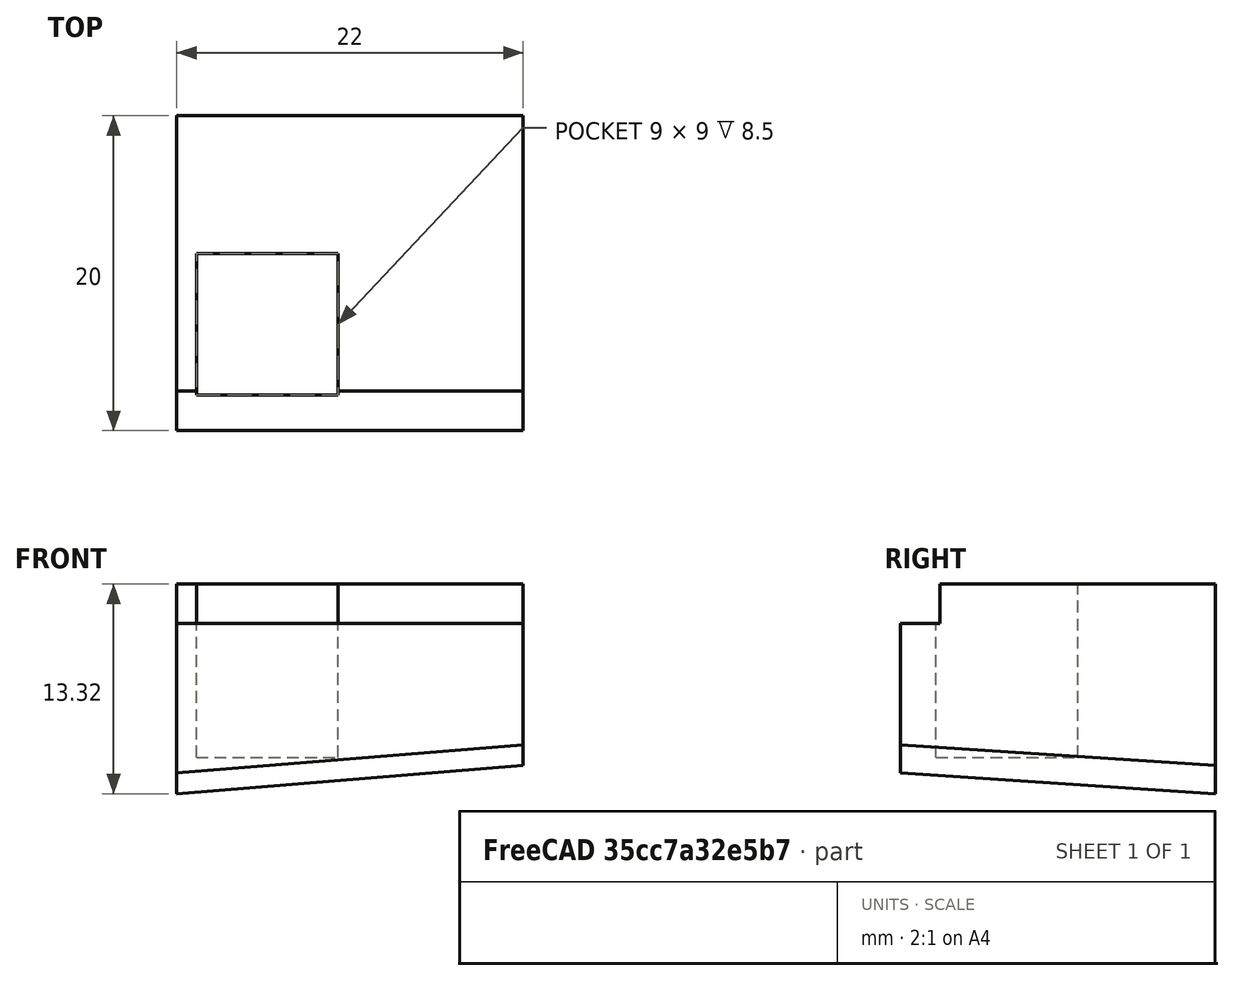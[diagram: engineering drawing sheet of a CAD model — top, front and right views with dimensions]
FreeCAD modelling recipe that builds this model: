
FCSTD DOCUMENT  (FreeCAD 0.16R6707 (Git))
Label: US_bracket_right
License: All rights reserved
LicenseURL: http://en.wikipedia.org/wiki/All_rights_reserved
objects: Part::Box×4, Part::Cut×3
note: 7 computed .brp shape members not serialized (recipe doc carries the construction recipe); baked Part::Feature solids carry a one-line shape summary decoded from their .brp

FEATURE [Part::Box] Box  label="Cube"
  Height = 15
  Length = 22
  Width = 20
FEATURE [Part::Box] Box001  label="Cube001"
  Height = 11
  Length = 9
  Placement = pos=(1.25,2.25,4) rot=(0,0,1;0rad)
  Width = 9
FEATURE [Part::Cut] Cut
  Base = -> Box
  Tool = -> Box001
FEATURE [Part::Box] Box002  label="Cube002"
  Height = 2.5
  Length = 22
  Placement = pos=(0,0,12.5) rot=(0,0,1;0rad)
  Width = 2.5
FEATURE [Part::Cut] Cut001
  Base = -> Cut
  Tool = -> Box002
FEATURE [Part::Box] Box003  label="Cube003"
  Height = 10
  Length = 24
  Placement = pos=(-1,-2,-7) rot=(-0.629505,-0.776997,0;0.10472rad)
  Width = 23
FEATURE [Part::Cut] Cut002
  Base = -> Cut001
  Tool = -> Box003
